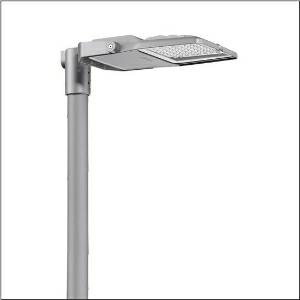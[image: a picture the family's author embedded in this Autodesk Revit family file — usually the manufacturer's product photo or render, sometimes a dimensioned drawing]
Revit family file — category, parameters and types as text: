
# Revit family: floodlight_fl_21_iq_mini___pl52_5xa7772c2d3a_4b1a
name_source: partatom
category: Lighting Fixtures
units: mm (PartAtom-declared; Revit-internal decimal feet)

## family parameters
Cut with Voids When Loaded = No
Host = Face
Light Source = No
Part Type = Normal
Room Calculation Point = No
Round Connector Dimension = Use Diameter
Shared = No

## types (1)
- --- (1 x LED, 12210 lm, 87.2 W, 3000K)
    Apparent Load = 87 VA
    CIE Flux Codes = 26 60 98 100 100
    Color Rendering = 70
    Color Temperature = 3000K
    Default Elevation = 1800 mm
    Description = Floodlight FL 21 iQ mini, floodlight, primary light control with lens, of PMMA, primary optical cover: protective disc, of toughened safety glass, transparent, light distribution: PL52, light emission: direct distribution, installation type: surface-mounted, lamps: LED, High Power LED, rated values: 12.210lm | 87,2W | 140lm/W (begin service life); end service life: 12.210lm | 92,1W; at 50% lumin. flux: 6.105lm | 40,1W | 152,2lm/W, colour temperature: 3000K, colour rendering: CRI > 70, light colour: 730, light setting 1 begin service life: 100% | 12.210lm | 87,2W | 140lm/W | 3.000K, light setting 1 end service life: 92,1W, further light settings possible, control: pre-setting: linear dimming characteristic, Auto-Match, Temp-Guard, Night-Set, Smart-Wire, Desk-Remote (wireless, voltage-free reading and setting of iQ features in the workshop via application-optimized NFC function/RFID function), optimised constant luminous flux control (CLO 2.0), Light-Fading, Lumen-Switch, with terminal, 6-pole, mains connection: 220..240V, AC, 50/60Hz, luminaire housing, of diecast aluminium, powder-coated, SITECO metallic grey (DB 702S), corrosivity category C5 mid according to DIN EN ISO 12944suitable for swimming poolschlorine-resistant, sealing non-destructively replaceable, please order mast flange separately, mast bracket, of steel, galvanised, powder-coated, protection rating (complete): IP66, insulation class (complete): insulation class II (safety insulation), certification: CE, ENEC, VDE, protection symbol: D, impact resistance: IK08, permissible operating ambient temperature: -40..+40°C, permissible operating ambient temperature for outdoor applications: -40..+50°C, standard: DIN EN 12944, LABS conformity tested according to VDMA 24364:2018-05, packaging unit: 1 piece

Light Distribution: PL52
    Height = 70 mm
    Lamp = 1 x LED
    Lamp Light Flux = 12210 lm
    Lamp Power = 87.2 W
    Lamp count = 1
    Length = 485 mm
    Luminous efficacy = 140 lm/W
    Manufacturer = Siteco
    ModVariant = No
    Model = 5XA7772C2D3A
    Number of Poles = 1
    OnlyDefault = Yes
    Power Factor = 1
    Product Name = Floodlight FL 21 iQ mini | PL52
    Product group = floodlight | pylon annexe
    ProductGroupID = 6201
    Protection Class = Protection class II
    Protection Degree = IP 66
    RLX_Detail_Level = 1
    RLX_Emergency_Light_Flux = 0 lm
    RLX_Emergency_Type = 0
    RLX_Emergency_Type_DB = No
    RlxData = <blob elided: 101697 chars, md5=c3398158>
    Socket = socket
    Standby Power = 0 W
    System Light Flux = 12210 lm
    System Power = 87 W
    Type Comments = factory setting: luminous flux: 100 % | dim-lin: 254 | 456 mA
    Type Image = l_1007125.jpg
    URL = http://relux.com
    VarID = @adj_163773
    Voltage = 0 V
    Weight = 0.00 kg
    Width = 337 mm

## geometry (parser evidence)
native form markers: Blend x4, Sweep x12
no freeform markers — native parametric forms only
